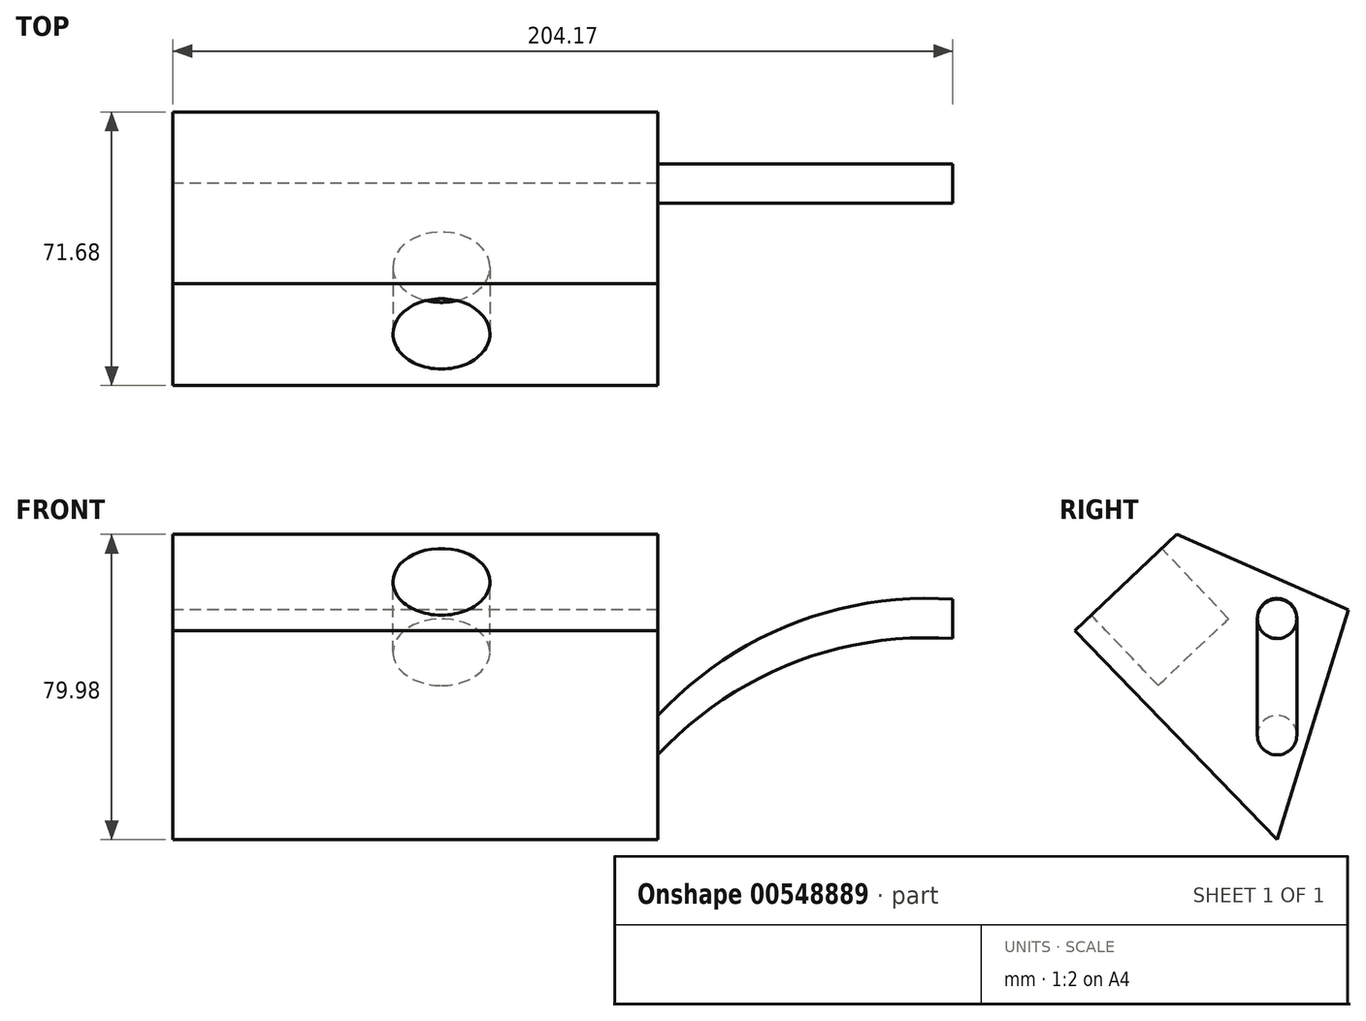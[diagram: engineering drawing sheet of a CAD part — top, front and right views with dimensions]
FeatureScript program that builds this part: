
annotation { "Feature Type Name" : "Feature", "Feature Type Description" : "" }
export const myFeature = defineFeature(function(context is Context, id is Id, definition is map)
    precondition{}
    {
        {
            var Q0;
            Q0=qCreatedBy(makeId("Right.planeOp"),FACE);
            var sketch = newSketch(context, id + "F0", { "sketchPlane" : qUnion([Q0])});
            skLineSegment(sketch, "E0", {"start": v(-52.98, 28.74) * mm, "end": v(-26.31, 54.01) * mm});
            skLineSegment(sketch, "E1", {"start": v(-26.31, 54.01) * mm, "end": v(18.7, 34.28) * mm});
            skLineSegment(sketch, "E2", {"start": v(18.7, 34.28) * mm, "end": v(0, -25.97) * mm});
            skLineSegment(sketch, "E3", {"start": v(0, -25.97) * mm, "end": v(-52.98, 28.74) * mm});
            skSolve(sketch);
        }
        {
            var Q0;
            Q0=makeQuery(id+"F0.imprint","IMPRINT",FACE,{"disambiguationData":[TD([[makeQuery(id+"F0.imprint","IMPRINT",EDGE,{"derivedFrom":sQuery(id+"F0.wireOp",EDGE,"E0")}),-1.0]])]});
            extrude(context, id + "F1", {"entities" : qUnion([Q0]), "depth" : 127 * mm, "offsetDistance" : 25.4 * mm});
        }
        {
            var Q0;
            Q0=makeQuery(id+"F1.opExtrude","SWEPT_FACE",FACE,{"disambiguationData":[OSD([sQuery(id+"F0.wireOp",EDGE,"E0")])]});
            var sketch = newSketch(context, id + "F2", { "sketchPlane" : qUnion([Q0])});
            skCircle(sketch, "E4", {"center": v(70.31, 0) * mm, "radius": 12.7 * mm});
            skSolve(sketch);
        }
        {
            var Q0;
            Q0 = qSketchRegion(id + "F2", true);
            extrude(context, id + "F3", {"entities" : qUnion([Q0]), "operationType" : NewBodyOperationType.REMOVE, "oppositeDirection" : true, "depth" : 25.4 * mm, "offsetDistance" : 25.4 * mm});
        }
        {
            var Q0;
            Q0=qCreatedBy(makeId("Front.planeOp"),FACE);
            var sketch = newSketch(context, id + "F4", { "sketchPlane" : qUnion([Q0])});
            skArc(sketch, "E5", {"start": v(204.17, 31.86) * mm, "mid": v(162.12, 25.4) * mm, "end": v(127, 1.38) * mm});
            skSolve(sketch);
        }
        {
            var Q0;
            Q0=makeQuery(id+"F1.opExtrude","CAP_FACE",FACE,{"disambiguationData":[OSD([sQuery(id+"F0.wireOp",EDGE,"E0"),sQuery(id+"F0.wireOp",EDGE,"E1"),sQuery(id+"F0.wireOp",EDGE,"E2"),sQuery(id+"F0.wireOp",EDGE,"E3")])],"isStart":false});
            var sketch = newSketch(context, id + "F5", { "sketchPlane" : qUnion([Q0])});
            skCircle(sketch, "E6", {"center": v(0, 1.38) * mm, "radius": 5.16 * mm});
            skSolve(sketch);
        }
        {
            var Q0;
            Q0=makeQuery(id+"F5.imprint","IMPRINT",FACE,{"disambiguationData":[TD([[makeQuery(id+"F5.imprint","IMPRINT",EDGE,{"derivedFrom":sQuery(id+"F5.wireOp",EDGE,"E6")}),1.0]])]});
            var Q1;
            Q1=sQuery(id+"F4.wireOp",EDGE,"E5");
            sweep(context, id + "F6", {"operationType" : NewBodyOperationType.ADD, "profiles" : qUnion([Q0]), "path" : qUnion([Q1]), "keepProfileOrientation" : true});
        }
    });
